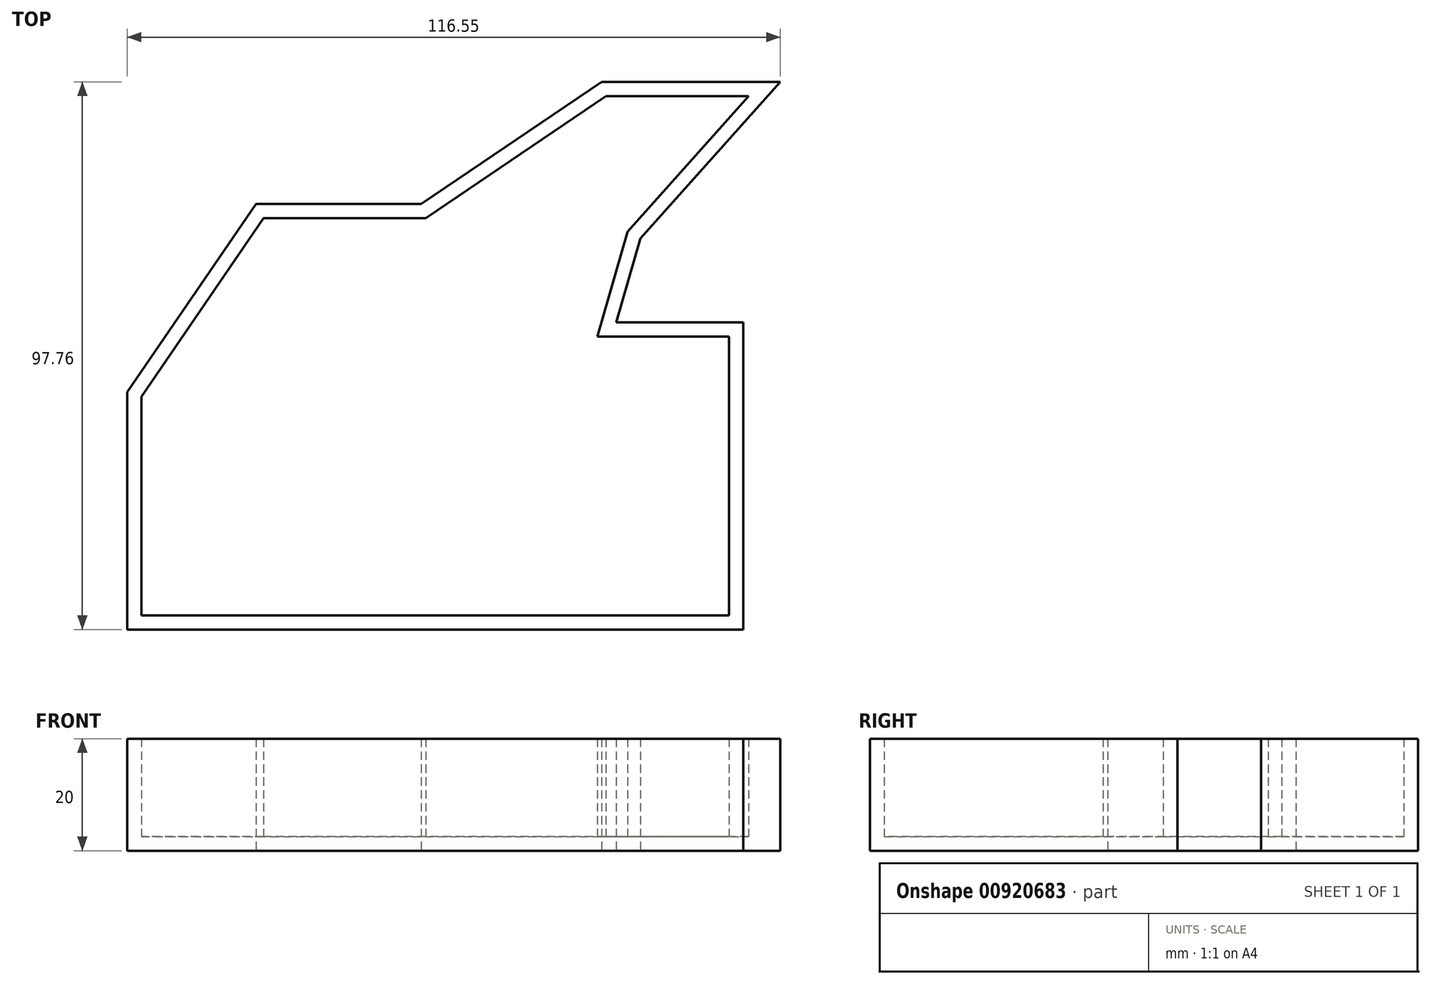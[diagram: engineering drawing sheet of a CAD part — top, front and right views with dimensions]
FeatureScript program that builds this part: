
annotation { "Feature Type Name" : "Feature", "Feature Type Description" : "" }
export const myFeature = defineFeature(function(context is Context, id is Id, definition is map)
    precondition{}
    {
        {
            var Q0;
            Q0=qCreatedBy(makeId("Top.planeOp"),FACE);
            var sketch = newSketch(context, id + "F0", { "sketchPlane" : qUnion([Q0])});
            skLineSegment(sketch, "E0", {"start": v(29.19, 27.41) * mm, "end": v(54.17, 55.38) * mm});
            skLineSegment(sketch, "E1", {"start": v(54.17, 55.38) * mm, "end": v(22.27, 55.38) * mm});
            skLineSegment(sketch, "E2", {"start": v(22.27, 55.38) * mm, "end": v(-9.89, 33.61) * mm});
            skLineSegment(sketch, "E3", {"start": v(-9.89, 33.61) * mm, "end": v(-39.4, 33.61) * mm});
            skLineSegment(sketch, "E4", {"start": v(-39.4, 33.61) * mm, "end": v(-62.38, 0) * mm});
            skLineSegment(sketch, "E5", {"start": v(-62.38, 0) * mm, "end": v(-62.38, -42.38) * mm});
            skLineSegment(sketch, "E6", {"start": v(-62.38, -42.38) * mm, "end": v(47.57, -42.38) * mm});
            skLineSegment(sketch, "E7", {"start": v(47.57, -42.38) * mm, "end": v(47.57, 12.47) * mm});
            skLineSegment(sketch, "E8", {"start": v(47.57, 12.47) * mm, "end": v(24.9, 12.47) * mm});
            skLineSegment(sketch, "E9", {"start": v(24.9, 12.47) * mm, "end": v(29.19, 27.41) * mm});
            skLineSegment(sketch, "E10", {"start": v(0, 0) * mm, "end": v(-32.18, -7.72) * mm});
            skSolve(sketch);
        }
        {
            var Q0;
            Q0=makeQuery(id+"F0.imprint","IMPRINT",FACE,{"disambiguationData":[TD([[makeQuery(id+"F0.imprint","IMPRINT",EDGE,{"derivedFrom":sQuery(id+"F0.wireOp",EDGE,"E0")}),1.0]])]});
            extrude(context, id + "F1", {"entities" : qUnion([Q0]), "depth" : 20 * mm, "offsetDistance" : 25.4 * mm});
        }
        {
            var Q0;
            Q0=makeQuery(id+"F1.opExtrude","CAP_FACE",FACE,{"disambiguationData":[OSD([sQuery(id+"F0.wireOp",EDGE,"E0"),sQuery(id+"F0.wireOp",EDGE,"E1"),sQuery(id+"F0.wireOp",EDGE,"E2"),sQuery(id+"F0.wireOp",EDGE,"E3"),sQuery(id+"F0.wireOp",EDGE,"E4"),sQuery(id+"F0.wireOp",EDGE,"E5"),sQuery(id+"F0.wireOp",EDGE,"E6"),sQuery(id+"F0.wireOp",EDGE,"E7"),sQuery(id+"F0.wireOp",EDGE,"E8"),sQuery(id+"F0.wireOp",EDGE,"E9")])],"isStart":false});
            shell(context, id + "F2", {"entities" : qUnion([Q0]), "thickness" : 2.54 * mm});
        }
    });
